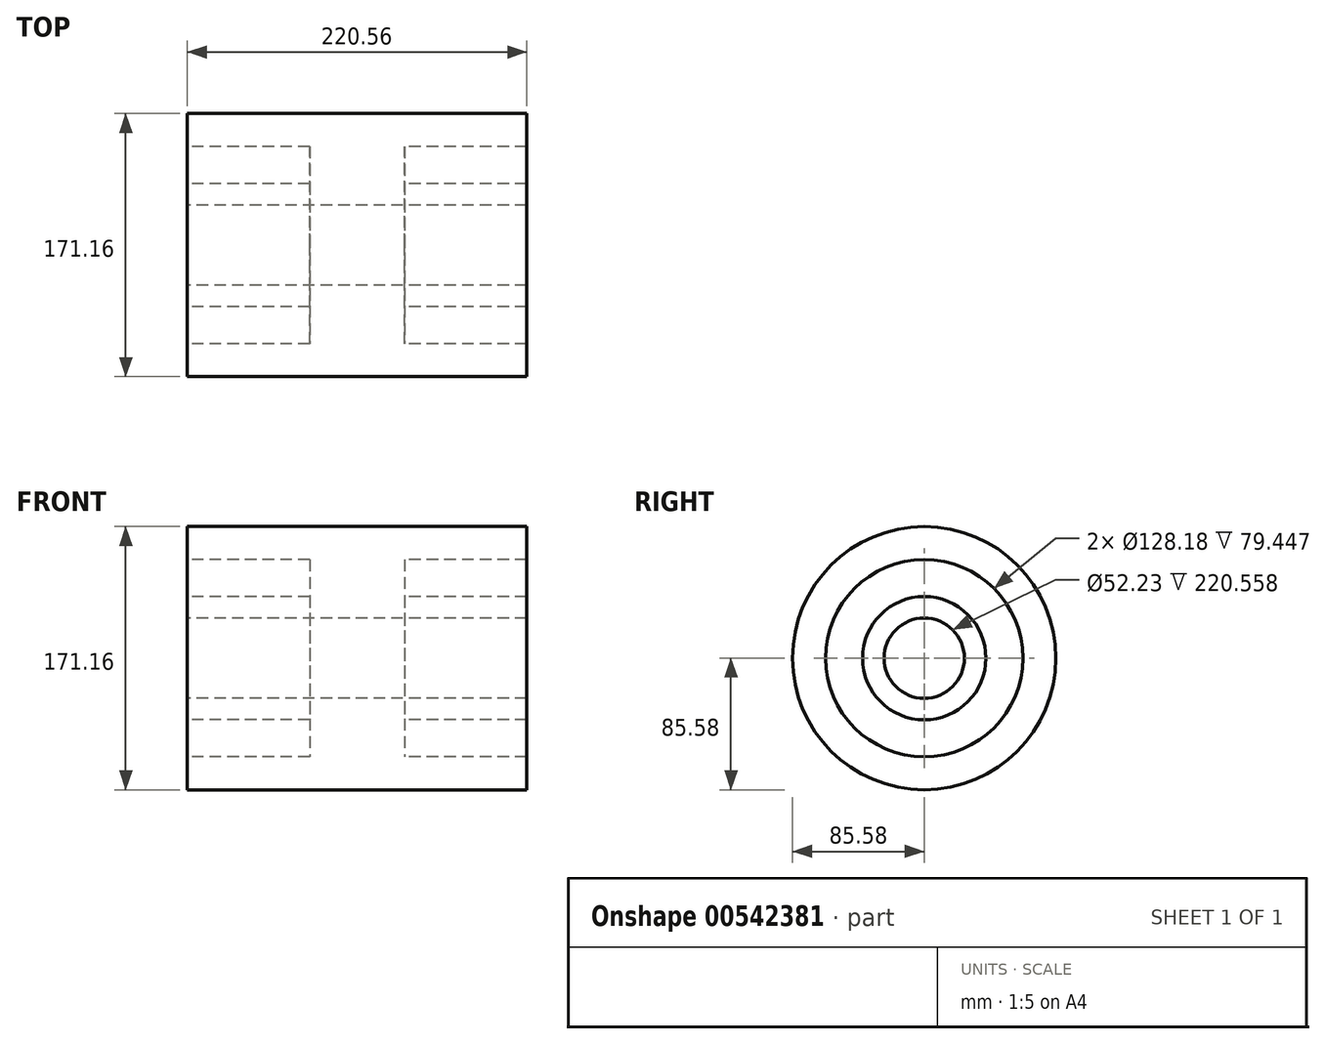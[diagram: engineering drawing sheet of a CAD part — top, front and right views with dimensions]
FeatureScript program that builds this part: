
annotation { "Feature Type Name" : "Feature", "Feature Type Description" : "" }
export const myFeature = defineFeature(function(context is Context, id is Id, definition is map)
    precondition{}
    {
        {
            var Q0;
            Q0=qCreatedBy(makeId("Front.planeOp"),FACE);
            var sketch = newSketch(context, id + "F0", { "sketchPlane" : qUnion([Q0])});
            skLineSegment(sketch, "E0", {"start": v(-92.09, 0) * mm, "end": v(95.79, 0) * mm, "construction": true});
            skLineSegment(sketch, "E1", {"start": v(0, 0) * mm, "end": v(0, 92.57) * mm, "construction": true});
            skLineSegment(sketch, "E2", {"start": v(0, 85.58) * mm, "end": v(110.28, 85.58) * mm});
            skLineSegment(sketch, "E3", {"start": v(110.28, 85.58) * mm, "end": v(110.28, 64.09) * mm});
            skLineSegment(sketch, "E4", {"start": v(110.28, 64.09) * mm, "end": v(30.83, 64.09) * mm});
            skLineSegment(sketch, "E5", {"start": v(30.83, 64.09) * mm, "end": v(30.83, 40.1) * mm});
            skLineSegment(sketch, "E6", {"start": v(30.83, 40.1) * mm, "end": v(110.28, 40.1) * mm});
            skLineSegment(sketch, "E7", {"start": v(110.28, 40.1) * mm, "end": v(110.28, 26.11) * mm});
            skLineSegment(sketch, "E8", {"start": v(110.28, 26.11) * mm, "end": v(0, 26.11) * mm});
            skLineSegment(sketch, "E9.MirrorCS", {"start": v(0, 85.58) * mm, "end": v(-110.28, 85.58) * mm});
            skLineSegment(sketch, "E10.MirrorCS", {"start": v(-110.28, 85.58) * mm, "end": v(-110.28, 64.09) * mm});
            skLineSegment(sketch, "E11.MirrorCS", {"start": v(-110.28, 64.09) * mm, "end": v(-30.83, 64.09) * mm});
            skLineSegment(sketch, "E12.MirrorCS", {"start": v(-30.83, 64.09) * mm, "end": v(-30.83, 40.1) * mm});
            skLineSegment(sketch, "E13.MirrorCS", {"start": v(-30.83, 40.1) * mm, "end": v(-110.28, 40.1) * mm});
            skLineSegment(sketch, "E14.MirrorCS", {"start": v(-110.28, 40.1) * mm, "end": v(-110.28, 26.11) * mm});
            skLineSegment(sketch, "E15.MirrorCS", {"start": v(-110.28, 26.11) * mm, "end": v(0, 26.11) * mm});
            skSolve(sketch);
        }
        {
            var Q0;
            Q0 = qSketchRegion(id + "F0", true);
            var Q1;
            Q1=sQuery(id+"F0.wireOp",EDGE,"E0");
            revolve(context, id + "F1", {"entities" : qUnion([Q0]), "axis" : qUnion([Q1]), "revolveType" : RevolveType.FULL});
        }
    });
